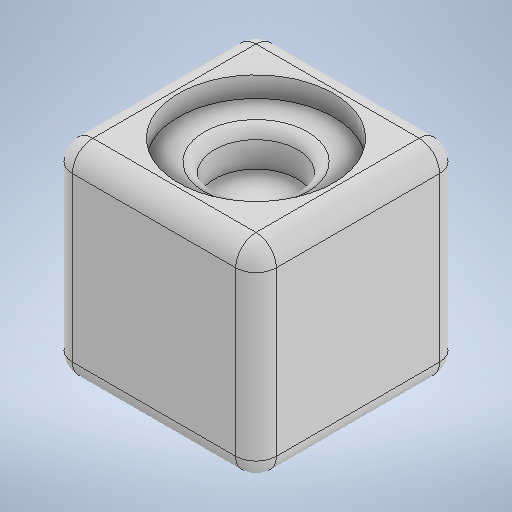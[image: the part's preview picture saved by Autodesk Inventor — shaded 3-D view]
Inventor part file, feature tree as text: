
AUTODESK INVENTOR PART (.ipt)
format: ipt  version: 2025 (Build 290162000, 162)  size: 305,664 bytes
history: native  units: in
note: dims shown in document units (in); Inventor stores cm internally (conversion verified against a paired STEP export)
features: extrude x7, sketch x7, fillet x5
ambient origin geometry x8: Origin, YZ Plane, XZ Plane, XY Plane, X Axis, Y Axis, Z Axis, Center Point
bodies: Solid1 (feature_tree)
feature tree (19):
  extrude  "Extrusion1"  Depth=0.7874in
  extrude  "Extrusion2"  Depth=0.7874in
  extrude  "Extrusion3"  Depth=0.3937in
  extrude  "Extrusion4"  Depth=0.0787in
  fillet  "Fillet1"  Radius=0.0787in
  extrude  "Extrusion5"  Depth=0.3937in
  extrude  "Extrusion6"  Depth=0.0787in TaperAngle=0.0deg
  extrude  "Extrusion7"  Depth=0.0394in
  fillet  "Fillet2"  Radius=0.1378in
  fillet  "Fillet3"  Radius=0.3134in
  fillet  "Fillet4"  Radius=0.1378in
  fillet  "Fillet5"  Radius=0.3205in
  sketch  "Sketch1"  dims[d0=0.7874in d1=0.7874in]
  sketch  "Sketch2"  dims[d2=0.7874in d3=0.0in d4=0.5984in]
  sketch  "Sketch3"  dims[d5=0.3937in d6=0.3937in]
  sketch  "Sketch4"  dims[d7=0.0787in d8=0.0in d9=0.5984in d10=0.0787in d11=0.0in]
  sketch  "Sketch5"  dims[d12=0.5984in d13=0.3937in]
  sketch  "Sketch6"  dims[d14=0.3937in d15=0.0787in d16=0.0in]
  sketch  "Sketch7"  dims[d17=0.0787in d18=0.3205in d19=0.1378in d20=0.0in d21=0.3134in d22=0.1378in d23=0.0in d24=0.3205in d25=0.1378in d26=0.0in d27=0.0787in d28=0.0394in d29=0.0394in d30=0.0394in]
